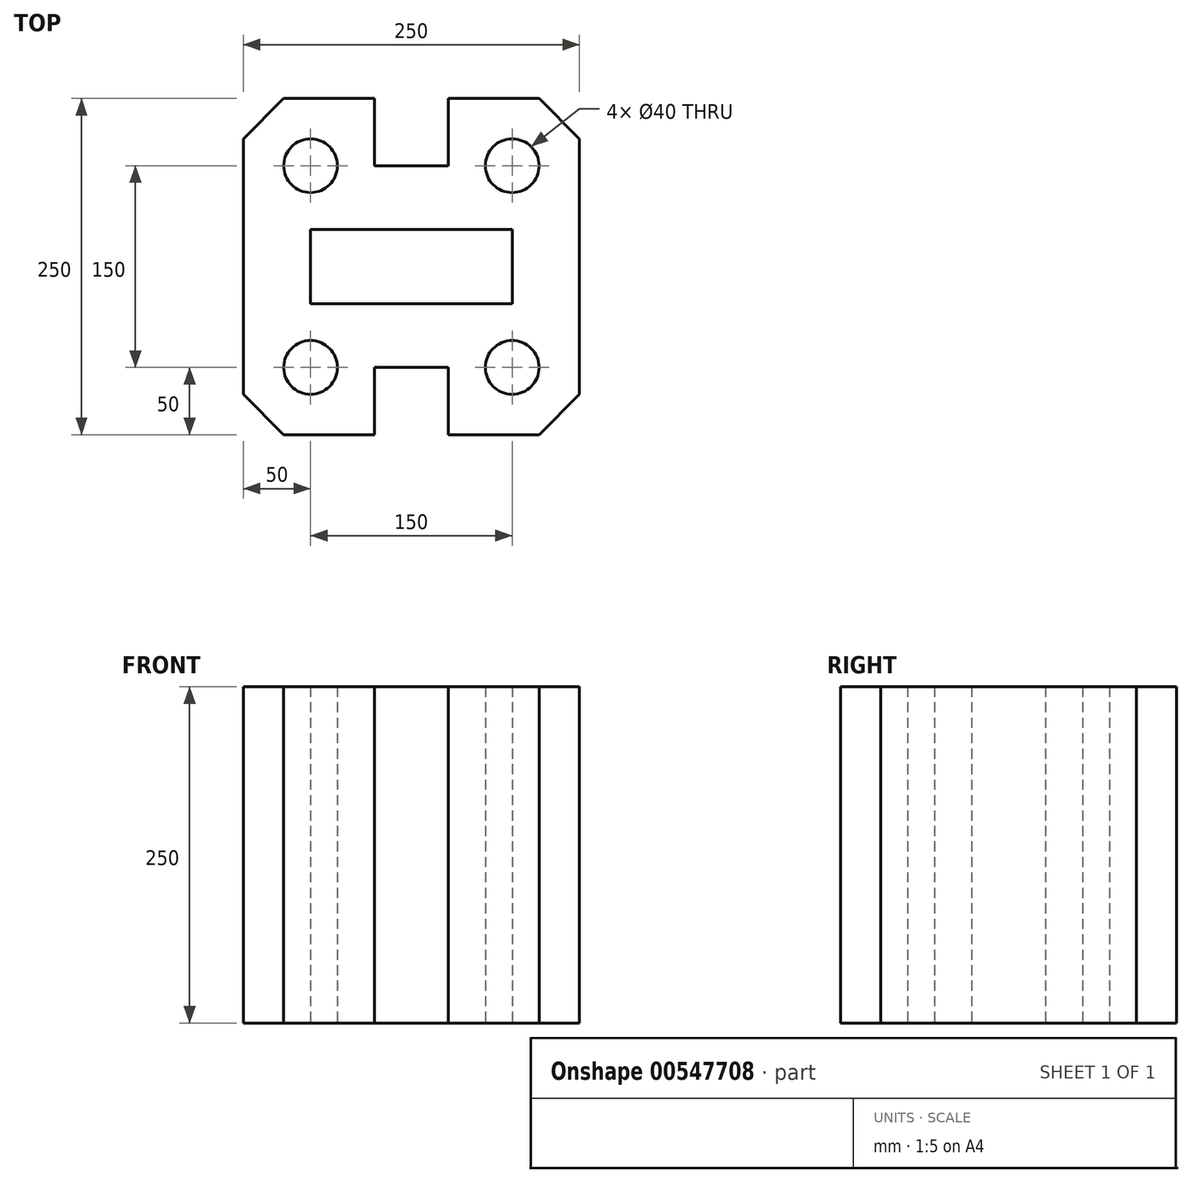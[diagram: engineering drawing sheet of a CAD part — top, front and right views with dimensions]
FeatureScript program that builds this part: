
annotation { "Feature Type Name" : "Feature", "Feature Type Description" : "" }
export const myFeature = defineFeature(function(context is Context, id is Id, definition is map)
    precondition{}
    {
        {
            var Q0;
            Q0=qCreatedBy(makeId("Top.planeOp"),FACE);
            var sketch = newSketch(context, id + "F0", { "sketchPlane" : qUnion([Q0])});
            skLineSegment(sketch, "E0.top", {"start": v(95, -125) * mm, "end": v(27.5, -125) * mm});
            skLineSegment(sketch, "E0.left", {"start": v(125, 95) * mm, "end": v(125, -95) * mm});
            skLineSegment(sketch, "E0.right", {"start": v(-125, 95) * mm, "end": v(-125, -95) * mm});
            skPoint(sketch, "E0.middle", {"position": v(0, 0) * mm});
            skLineSegment(sketch, "E1.bottom", {"start": v(75, 27.5) * mm, "end": v(-75, 27.5) * mm});
            skLineSegment(sketch, "E1.top", {"start": v(75, -27.5) * mm, "end": v(-75, -27.5) * mm});
            skLineSegment(sketch, "E1.left", {"start": v(75, 27.5) * mm, "end": v(75, -27.5) * mm});
            skLineSegment(sketch, "E1.right", {"start": v(-75, 27.5) * mm, "end": v(-75, -27.5) * mm});
            skLineSegment(sketch, "E2", {"start": v(0, 0) * mm, "end": v(0, 125) * mm, "construction": true});
            skLineSegment(sketch, "E3", {"start": v(0, 0) * mm, "end": v(125, 0) * mm, "construction": true});
            skLineSegment(sketch, "E4.top", {"start": v(27.5, 75) * mm, "end": v(-27.5, 75) * mm});
            skLineSegment(sketch, "E4.left", {"start": v(27.5, 125) * mm, "end": v(27.5, 75) * mm});
            skLineSegment(sketch, "E4.right", {"start": v(-27.5, 125) * mm, "end": v(-27.5, 75) * mm});
            skPoint(sketch, "E4.middle", {"position": v(0, 100) * mm});
            skLineSegment(sketch, "E5.trimOffspring", {"start": v(-27.5, 125) * mm, "end": v(-95, 125) * mm});
            skLineSegment(sketch, "E6", {"start": v(27.5, 125) * mm, "end": v(95, 125) * mm});
            skLineSegment(sketch, "E7.MirrorCS", {"start": v(27.5, -125) * mm, "end": v(27.5, -75) * mm});
            skLineSegment(sketch, "E8.MirrorCS", {"start": v(-27.5, -125) * mm, "end": v(-27.5, -75) * mm});
            skLineSegment(sketch, "E9.MirrorCS", {"start": v(27.5, -75) * mm, "end": v(-27.5, -75) * mm});
            skLineSegment(sketch, "E10.trimOffspring", {"start": v(-27.5, -125) * mm, "end": v(-95, -125) * mm});
            skLineSegment(sketch, "E11", {"start": v(-95, 125) * mm, "end": v(-125, 95) * mm});
            skLineSegment(sketch, "E12", {"start": v(-95, -125) * mm, "end": v(-125, -95) * mm});
            skLineSegment(sketch, "E13", {"start": v(125, -95) * mm, "end": v(95, -125) * mm});
            skLineSegment(sketch, "E14", {"start": v(95, 125) * mm, "end": v(125, 95) * mm});
            skPoint(sketch, "E15.orphan", {"position": v(-125, -125) * mm});
            skPoint(sketch, "E16.orphan", {"position": v(125, -125) * mm});
            skPoint(sketch, "E17.orphan", {"position": v(125, 125) * mm});
            skPoint(sketch, "E18.orphan", {"position": v(-125, 125) * mm});
            skCircle(sketch, "E19", {"center": v(-75, 75) * mm, "radius": 20 * mm});
            skCircle(sketch, "E20", {"center": v(-75, -75) * mm, "radius": 20 * mm});
            skCircle(sketch, "E21", {"center": v(75, -75) * mm, "radius": 20 * mm});
            skCircle(sketch, "E22", {"center": v(75, 75) * mm, "radius": 20 * mm});
            skSolve(sketch);
        }
        {
            var Q0;
            Q0=qSketchRegion(id+"F0",true);
            extrude(context, id + "F1", {"entities" : qUnion([Q0]), "endBound" : BoundingType.SYMMETRIC, "depth" : 250 * mm, "offsetDistance" : 25 * mm});
        }
    });
